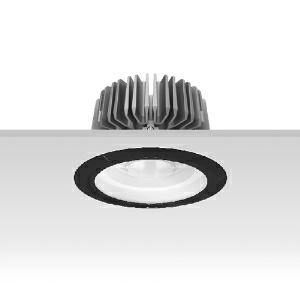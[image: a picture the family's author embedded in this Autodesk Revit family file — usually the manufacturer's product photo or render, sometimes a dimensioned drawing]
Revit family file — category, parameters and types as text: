
# Revit family: 3f_filippi_-_3f_reno_bianco_ampio_3f_filippi_-_30349_a01024_-_3f_reno_150_wh_3000-840_wide___vt_bk_3dde
name_source: partatom
category: Lighting Fixtures
units: mm (PartAtom-declared; Revit-internal decimal feet)

## family parameters
Cut with Voids When Loaded = No
Host = Face
Light Source = No
Part Type = Normal
Room Calculation Point = No
Round Connector Dimension = Use Diameter
Shared = No

## types (1)
- 3F Filippi - 3F Reno Bianco Ampio (1 x LED, 2647 lm, 28 W, 4000 K)
    Apparent Load = 28 VA
    Approval mark = CE
    CIE Flux Codes = 74 93 99 100 100
    Color Rendering = 80
    Color Temperature = 4000 K
    Control Gear = Electronic ballast
    Default Elevation = 1800 mm
    Description = ILLUMINOTECHNICAL
Luminous efficiency 100% (DLOR 100%, ULOR 0%).
Initial luminous flux of the luminaire 2647 lm.
Direct symmetric wide distribution.
Installation Interdistance Transv.D = 1.54 x hu - Long.D = 1.54 x hu.
Tabular UGR (CIE 117 - 4H-8H; S=0.25H; 70/50/20): RUG 24.4 - 24.2.
Beam angle: 74° - 73°.
Luminous efficacy 95 lm/W.
Lifetime (L90/B10): 30000 h. (tq+25°C)
Lifetime (L85/B10): 50000 h. (tq+25°C)
Lifetime (L70/B10): 80000 h. (tq+25°C)
Sudden decreased luminous flux after 50000 hours: 0% (C0).
Photobiological safety in compliance with IEC/TR 62778: RG0 risk exempt, (IEC 62471).
In compliance with IEC/EN 62722-2-1 - IEC/EN 62717 standards.

SOURCE
Compact LED module 3000/840.
Energy efficiency class (UE 2019/2020 - UE 2019/2015): D.
CIE 13.3 Colour rendering index: CRI >80 (R9 <50%).
IES TM-30 Fidelity Index: Rf = 84 Rg = 95.
CCT nominal colour temperature 4000 K.
Colour initial tolerance (MacAdam): SDCM 3.
Zhaga Book 3 compliant.

MECHANICAL
Passive heat dissipator in die-casting aluminium, oversized, for optimum thermal management of the LED module.
Parabolic element with graduated/concentric rings in white polycarbonate.
Transparent external lens with glossy and satin differentiated surfaces, with a cooling and anti-insect system in methacrylate (PMMA).
Fastening spring clips in stainless steel.
Dimensions: diameter 176 mm, height 111 mm. Weight 1.45 kg.
IP44 protection degree for exposed part, IP20 for recessed part.
Mechanical strength to impacts IK06 (1 joule).
Glow-wire test resistance 650°C.

ELECTRICAL
Wiring on a separate unit.
Halogen Free electronic wiring 230V-50/60Hz, power factor 0.95, THD <25%, constant output current, SELV, class II, 1 driver.
Power of the luminaire 28 W.
ENEC - CE.
SAFE FLICKER: PstLM=<1 and SVM=<0.4 (IEC TR 61547-1 and IEC TR 63158), to ensure a more comfortable and safe light.
Luminaire compliant with EN 60598-2-22 for power supply from a centralised emergency system CPSS (Central Power Supply System), not incorporated in the luminaire - high risk areas excluded. The default power and flux are 100% in AC and 100% in DC.
Ambient temperature from 0°C to +25°C.
Temperature class T6 max 85°C.
Relative humidity UR: <85%.

INSTALLATION
Pull-up recessed fitting.
False ceiling carving: 150 mm.
All accessories dedicated to this product are available on the Catalog and on our website www.3F-Filippi.com.

ACCESSORIES
A01024 - VT transparent glass, tempered, not flammable, locked and in line with the trim, in black polycarbonate.

APPLICATIONS
Environments: architectural, commercial, exhibition areas, transit areas, corridors, shops, display windows, service areas.
In false ceilings with narrow voids.

WARNING
Luminaire designed for disposal/recycling at end-of-life.
Replaceable (LED only) light source by a professional. Replaceable control gear by a professional.
    Height = 0 mm  [stored 0 ft]
    Lamp = 1 x LED
    Lamp Light Flux = 2647 lm
    Lamp Power = 28 W
    Lamp count = 1
    Length = 176 mm
    Lifetime = 50000 h
    Luminous efficacy = 95 lm/W
    Manufacturer = 3F Filippi
    ModVariant = No
    Model = 3F Filippi - 30349+A01024 - 3F Reno 150 WH 3000-840 WIDE + VT BK
    Mounting Place = Ceiling
    Mounting Type = Recessed
    Number of Poles = 1
    OnlyDefault = Yes
    Power Factor = 1
    Product Name = 3F Filippi - 3F Reno Bianco Ampio
    Product group = recessed luminaire
    ProductGroupID = 4
    Protection Class = Protection class II
    Protection Degree = IP 20
    RLX_Detail_Level = 1
    RLX_Emergency_Light_Flux = 0 lm
    RLX_Emergency_Type = 0
    RLX_Emergency_Type_DB = No
    RlxData = <blob elided: 88553 chars, md5=6d071107>
    Socket = socket
    Standby Power = 0 W
    System Light Flux = 2647 lm
    System Power = 28 W
    Type Comments = Product without accessories
    Type Image = 3ffilippi_3f_reno_150_wh_d150__a01024.jpg
    URL = http://relux.com
    VarID = ---
    Voltage = 0 V
    Weight = 0.00 kg
    Width = 0 mm  [stored 0 ft]

note: [stored X ft] marks values corroborated as IEEE doubles in the binary element streams (Revit-internal decimal feet)

## geometry (parser evidence)
native form markers: Blend x4, Sweep x12
no freeform markers — native parametric forms only
